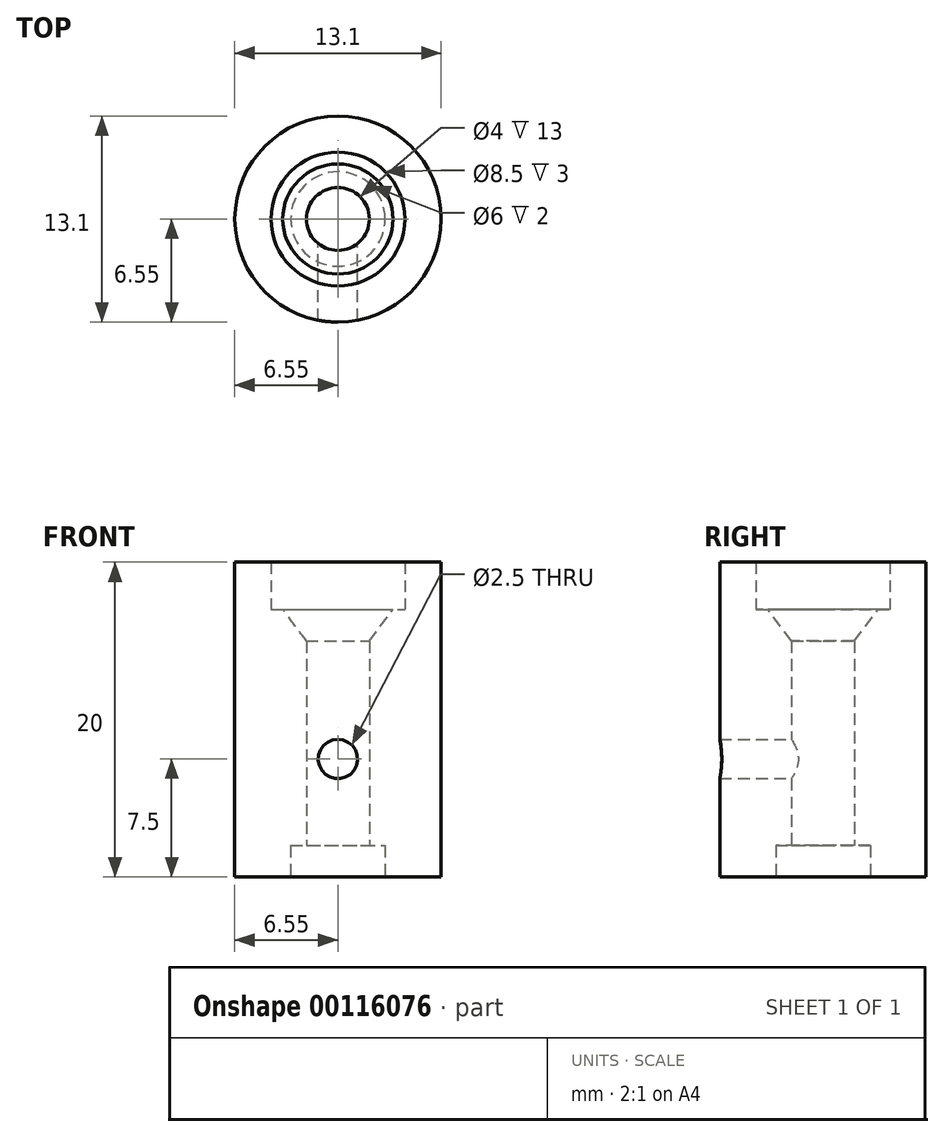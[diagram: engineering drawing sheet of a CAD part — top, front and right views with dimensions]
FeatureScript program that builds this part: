
annotation { "Feature Type Name" : "Feature", "Feature Type Description" : "" }
export const myFeature = defineFeature(function(context is Context, id is Id, definition is map)
    precondition{}
    {
        {
            var Q0;
            Q0=qCreatedBy(makeId("Front.planeOp"),FACE);
            var sketch = newSketch(context, id + "F0", { "sketchPlane" : qUnion([Q0])});
            skLineSegment(sketch, "E0", {"start": v(0, 0) * mm, "end": v(0, 34.45) * mm, "construction": true});
            skLineSegment(sketch, "E1", {"start": v(-2, 17) * mm, "end": v(-4.25, 17) * mm});
            skLineSegment(sketch, "E2", {"start": v(-4.25, 17) * mm, "end": v(-4.25, 20) * mm});
            skLineSegment(sketch, "E3", {"start": v(-4.25, 20) * mm, "end": v(-6.55, 20) * mm});
            skLineSegment(sketch, "E4", {"start": v(-6.55, 20) * mm, "end": v(-6.55, 0) * mm});
            skLineSegment(sketch, "E5", {"start": v(-6.55, 0) * mm, "end": v(-3, 0) * mm});
            skLineSegment(sketch, "E6", {"start": v(-2, 2) * mm, "end": v(-2, 17) * mm});
            skLineSegment(sketch, "E7", {"start": v(-3, 0) * mm, "end": v(-3, 2) * mm});
            skLineSegment(sketch, "E8", {"start": v(-3, 2) * mm, "end": v(-2, 2) * mm});
            skPoint(sketch, "E9.orphan", {"position": v(-2, 0) * mm});
            skLineSegment(sketch, "E10", {"start": v(-3.5, 17) * mm, "end": v(-2, 15) * mm});
            skSolve(sketch);
        }
        {
            var Q0;
            {var subQ0=sQuery(id+"F0.wireOp",EDGE,"E2");Q0=makeQuery(id+"F0.imprint","IMPRINT",FACE,{"disambiguationData":[TD([[makeQuery(id+"F0.imprint","IMPRINT",EDGE,{"derivedFrom":subQ0}),1.0]])]});}
            var Q1;
            Q1=sQuery(id+"F0.wireOp",EDGE,"E0");
            revolve(context, id + "F1", {"entities" : qUnion([Q0]), "axis" : qUnion([Q1]), "revolveType" : RevolveType.FULL});
        }
        {
            var Q0;
            Q0=qCreatedBy(makeId("Front.planeOp"),FACE);
            var sketch = newSketch(context, id + "F2", { "sketchPlane" : qUnion([Q0])});
            skCircle(sketch, "E11", {"center": v(0, 7.5) * mm, "radius": 1.25 * mm});
            skSolve(sketch);
        }
        {
            var Q0;
            Q0 = qSketchRegion(id + "F2", true);
            extrude(context, id + "F3", {"entities" : qUnion([Q0]), "operationType" : NewBodyOperationType.REMOVE, "depth" : 12.6 * mm});
        }
    });
